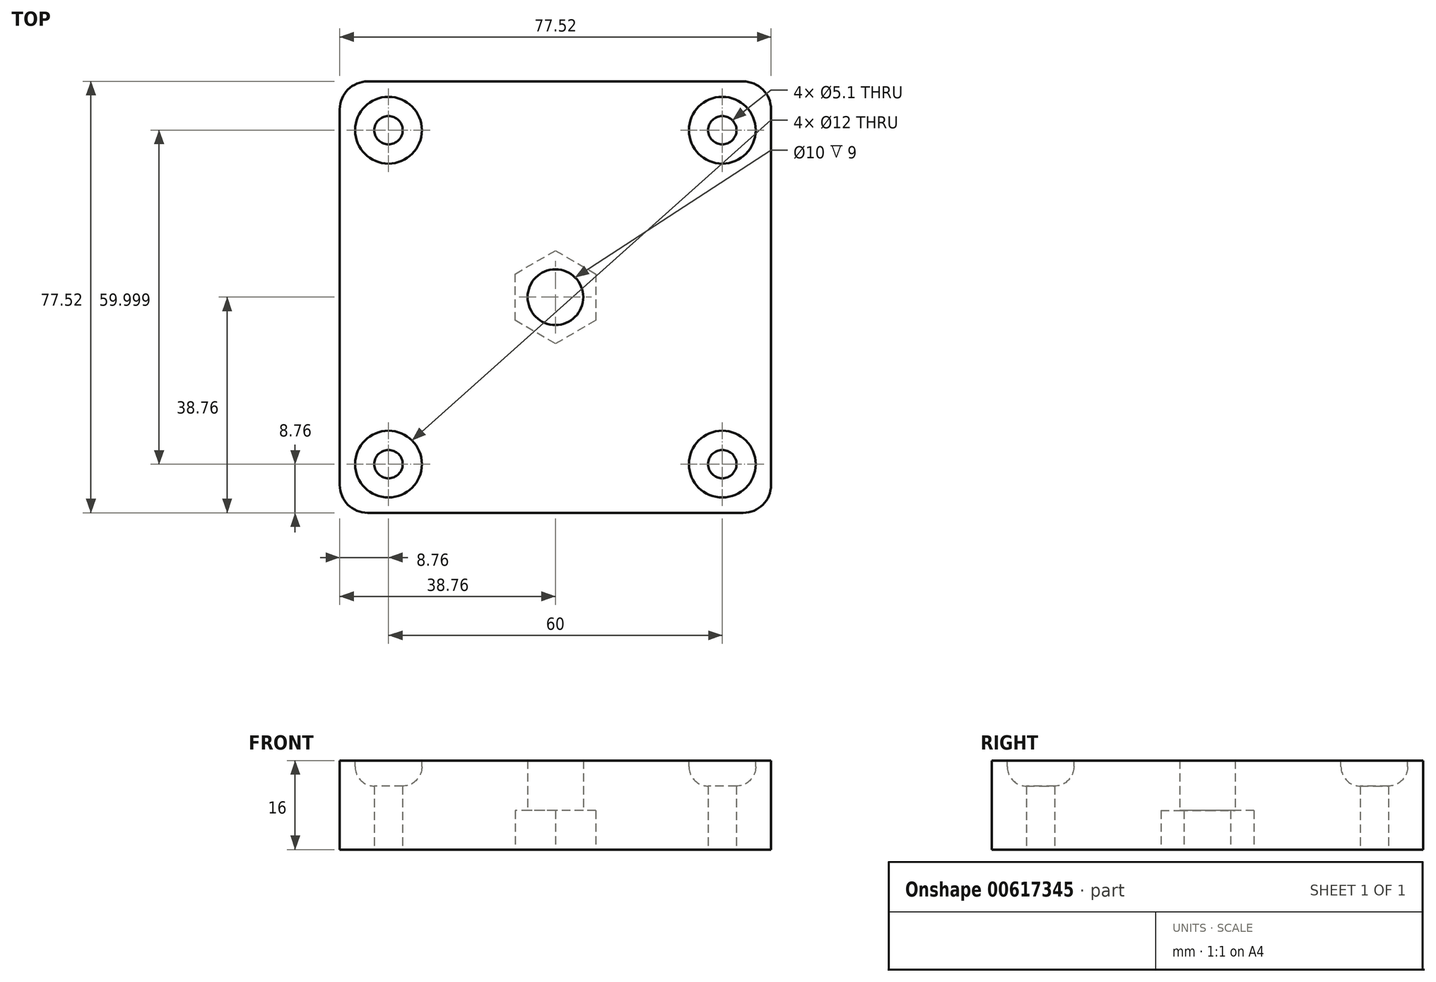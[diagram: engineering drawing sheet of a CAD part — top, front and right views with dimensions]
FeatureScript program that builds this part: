
annotation { "Feature Type Name" : "Feature", "Feature Type Description" : "" }
export const myFeature = defineFeature(function(context is Context, id is Id, definition is map)
    precondition{}
    {
        {
            var Q0;
            Q0=qCreatedBy(makeId("Top.planeOp"),FACE);
            var sketch = newSketch(context, id + "F0", { "sketchPlane" : qUnion([Q0])});
            skLineSegment(sketch, "E0.bottom", {"start": v(38.75, 38.76) * mm, "end": v(-38.76, 38.76) * mm});
            skLineSegment(sketch, "E0.top", {"start": v(38.76, -38.76) * mm, "end": v(-38.76, -38.76) * mm});
            skLineSegment(sketch, "E0.left", {"start": v(38.75, 38.76) * mm, "end": v(38.76, -38.76) * mm});
            skLineSegment(sketch, "E0.right", {"start": v(-38.76, 38.76) * mm, "end": v(-38.75, -38.76) * mm});
            skPoint(sketch, "E0.middle", {"position": v(0, 0) * mm});
            skCircle(sketch, "E1", {"center": v(-30, -30) * mm, "radius": 2.55 * mm});
            skCircle(sketch, "E2", {"center": v(30, -30) * mm, "radius": 2.55 * mm});
            skCircle(sketch, "E3", {"center": v(-30, 30) * mm, "radius": 2.55 * mm});
            skCircle(sketch, "E4", {"center": v(30, 30) * mm, "radius": 2.55 * mm});
            skCircle(sketch, "E5.cCircle", {"center": v(0, 0) * mm, "radius": 8.37 * mm, "construction": true});
            skLineSegment(sketch, "E5.0", {"start": v(0, -8.37) * mm, "end": v(-7.25, -4.19) * mm});
            skLineSegment(sketch, "E5.1", {"start": v(-7.25, -4.19) * mm, "end": v(-7.25, 4.19) * mm});
            skLineSegment(sketch, "E5.2", {"start": v(-7.25, 4.19) * mm, "end": v(0, 8.37) * mm});
            skLineSegment(sketch, "E5.3", {"start": v(0, 8.37) * mm, "end": v(7.25, 4.19) * mm});
            skLineSegment(sketch, "E5.4", {"start": v(7.25, 4.19) * mm, "end": v(7.25, -4.19) * mm});
            skLineSegment(sketch, "E5.5", {"start": v(7.25, -4.19) * mm, "end": v(0, -8.37) * mm});
            skCircle(sketch, "E6", {"center": v(0, 0) * mm, "radius": 5 * mm});
            skSolve(sketch);
        }
        {
            var Q0;
            Q0=makeQuery(id+"F0.imprint","IMPRINT",FACE,{"disambiguationData":[TD([[makeQuery(id+"F0.imprint","IMPRINT",EDGE,{"derivedFrom":sQuery(id+"F0.wireOp",EDGE,"E0.bottom")}),1.0]])]});
            var Q1;
            Q1=makeQuery(id+"F0.imprint","IMPRINT",FACE,{"disambiguationData":[TD([[makeQuery(id+"F0.imprint","IMPRINT",EDGE,{"derivedFrom":sQuery(id+"F0.wireOp",EDGE,"IMMJGL6N-8Sgl-opJO-aPiA-doJnAwbAfOUA.bottom")}),-1.0]])]});
            var Q2;
            Q2=makeQuery(id+"F0.imprint","IMPRINT",FACE,{"disambiguationData":[TD([[makeQuery(id+"F0.imprint","IMPRINT",EDGE,{"derivedFrom":sQuery(id+"F0.wireOp",EDGE,"E5.0")}),-1.0]])]});
            extrude(context, id + "F1", {"entities" : qUnion([Q0, Q1, Q2]), "depth" : 16 * mm, "offsetDistance" : 25 * mm});
        }
        {
            var Q0;
            Q0=makeQuery(id+"F0.imprint","IMPRINT",FACE,{"disambiguationData":[TD([[makeQuery(id+"F0.imprint","IMPRINT",EDGE,{"derivedFrom":sQuery(id+"F0.wireOp",EDGE,"IMMJGL6N-8Sgl-opJO-aPiA-doJnAwbAfOUA.bottom")}),-1.0]])]});
            var Q1;
            Q1=makeQuery(id+"F0.imprint","IMPRINT",FACE,{"disambiguationData":[TD([[makeQuery(id+"F0.imprint","IMPRINT",EDGE,{"derivedFrom":sQuery(id+"F0.wireOp",EDGE,"E5.0")}),-1.0]])]});
            extrude(context, id + "F2", {"entities" : qUnion([Q0, Q1]), "operationType" : NewBodyOperationType.REMOVE, "depth" : 7 * mm, "offsetDistance" : 25 * mm});
        }
        {
            var Q0;
            Q0=makeQuery(id+"F1.opExtrude","SWEPT_EDGE",EDGE,{"disambiguationData":[OSD([sQuery(id+"F0.wireOp",EDGE,"E0.top"),sQuery(id+"F0.wireOp",EDGE,"E0.left")])]});
            var Q1;
            Q1=makeQuery(id+"F1.opExtrude","SWEPT_EDGE",EDGE,{"disambiguationData":[OSD([sQuery(id+"F0.wireOp",EDGE,"E0.top"),sQuery(id+"F0.wireOp",EDGE,"E0.right")])]});
            var Q2;
            Q2=makeQuery(id+"F1.opExtrude","SWEPT_EDGE",EDGE,{"disambiguationData":[OSD([sQuery(id+"F0.wireOp",EDGE,"E0.bottom"),sQuery(id+"F0.wireOp",EDGE,"E0.left")])]});
            var Q3;
            Q3=makeQuery(id+"F1.opExtrude","SWEPT_EDGE",EDGE,{"disambiguationData":[OSD([sQuery(id+"F0.wireOp",EDGE,"E0.bottom"),sQuery(id+"F0.wireOp",EDGE,"E0.right")])]});
            fillet(context, id + "F3", {"entities" : qUnion([Q0, Q1, Q2, Q3]), "radius" : 5 * mm, "tangentPropagation" : true, "allowEdgeOverflow" : false});
        }
        {
            var Q0;
            Q0=makeQuery(id+"F1.opExtrude","CAP_FACE",FACE,{"disambiguationData":[OSD([sQuery(id+"F0.wireOp",EDGE,"E0.bottom"),sQuery(id+"F0.wireOp",EDGE,"E0.top"),sQuery(id+"F0.wireOp",EDGE,"E0.left"),sQuery(id+"F0.wireOp",EDGE,"E0.right"),sQuery(id+"F0.wireOp",EDGE,"E1"),sQuery(id+"F0.wireOp",EDGE,"E2"),sQuery(id+"F0.wireOp",EDGE,"E3"),sQuery(id+"F0.wireOp",EDGE,"E4"),sQuery(id+"F0.wireOp",EDGE,"E5.0"),sQuery(id+"F0.wireOp",EDGE,"E5.1"),sQuery(id+"F0.wireOp",EDGE,"E5.2"),sQuery(id+"F0.wireOp",EDGE,"E5.3"),sQuery(id+"F0.wireOp",EDGE,"E5.4"),sQuery(id+"F0.wireOp",EDGE,"E5.5")])],"isStart":false});
            var sketch = newSketch(context, id + "F4", { "sketchPlane" : qUnion([Q0])});
            skCircle(sketch, "E7", {"center": v(-30, 30) * mm, "radius": 6 * mm});
            skCircle(sketch, "E8", {"center": v(30, 30) * mm, "radius": 6 * mm});
            skCircle(sketch, "E9", {"center": v(30, -30) * mm, "radius": 6 * mm});
            skCircle(sketch, "E10", {"center": v(-30, -30) * mm, "radius": 6 * mm});
            skSolve(sketch);
        }
        {
            var Q0;
            Q0=makeQuery(id+"F4.imprint","IMPRINT",FACE,{"disambiguationData":[TD([[makeQuery(id+"F4.imprint","IMPRINT",EDGE,{"derivedFrom":sQuery(id+"F4.wireOp",EDGE,"E7")}),1.0]])]});
            var Q1;
            Q1=makeQuery(id+"F4.imprint","IMPRINT",FACE,{"disambiguationData":[TD([[makeQuery(id+"F4.imprint","IMPRINT",EDGE,{"derivedFrom":sQuery(id+"F4.wireOp",EDGE,"E8")}),1.0]])]});
            var Q2;
            Q2=makeQuery(id+"F4.imprint","IMPRINT",FACE,{"disambiguationData":[TD([[makeQuery(id+"F4.imprint","IMPRINT",EDGE,{"derivedFrom":sQuery(id+"F4.wireOp",EDGE,"E9")}),1.0]])]});
            var Q3;
            Q3=makeQuery(id+"F4.imprint","IMPRINT",FACE,{"disambiguationData":[TD([[makeQuery(id+"F4.imprint","IMPRINT",EDGE,{"derivedFrom":sQuery(id+"F4.wireOp",EDGE,"E10")}),1.0]])]});
            extrude(context, id + "F5", {"entities" : qUnion([Q0, Q1, Q2, Q3]), "operationType" : NewBodyOperationType.REMOVE, "oppositeDirection" : true, "depth" : 4.6 * mm, "offsetDistance" : 25 * mm});
        }
        {
            var Q0;
            Q0=makeQuery(id+"F5.boolean.opBoolean","COPY",EDGE,{"derivedFrom":makeQuery(id+"F5.opExtrude","CAP_EDGE",EDGE,{"disambiguationData":[OSD([sQuery(id+"F4.wireOp",EDGE,"E10")])],"isStart":false})});
            var Q1;
            Q1=makeQuery(id+"F5.boolean.opBoolean","COPY",EDGE,{"derivedFrom":makeQuery(id+"F5.opExtrude","CAP_EDGE",EDGE,{"disambiguationData":[OSD([sQuery(id+"F4.wireOp",EDGE,"E7")])],"isStart":false})});
            var Q2;
            Q2=makeQuery(id+"F5.boolean.opBoolean","COPY",EDGE,{"derivedFrom":makeQuery(id+"F5.opExtrude","CAP_EDGE",EDGE,{"disambiguationData":[OSD([sQuery(id+"F4.wireOp",EDGE,"E9")])],"isStart":false})});
            var Q3;
            Q3=makeQuery(id+"F5.boolean.opBoolean","COPY",EDGE,{"derivedFrom":makeQuery(id+"F5.opExtrude","CAP_EDGE",EDGE,{"disambiguationData":[OSD([sQuery(id+"F4.wireOp",EDGE,"E8")])],"isStart":false})});
            fillet(context, id + "F6", {"entities" : qUnion([Q0, Q1, Q2, Q3]), "radius" : 3.5 * mm, "tangentPropagation" : true, "allowEdgeOverflow" : false});
        }
    });
